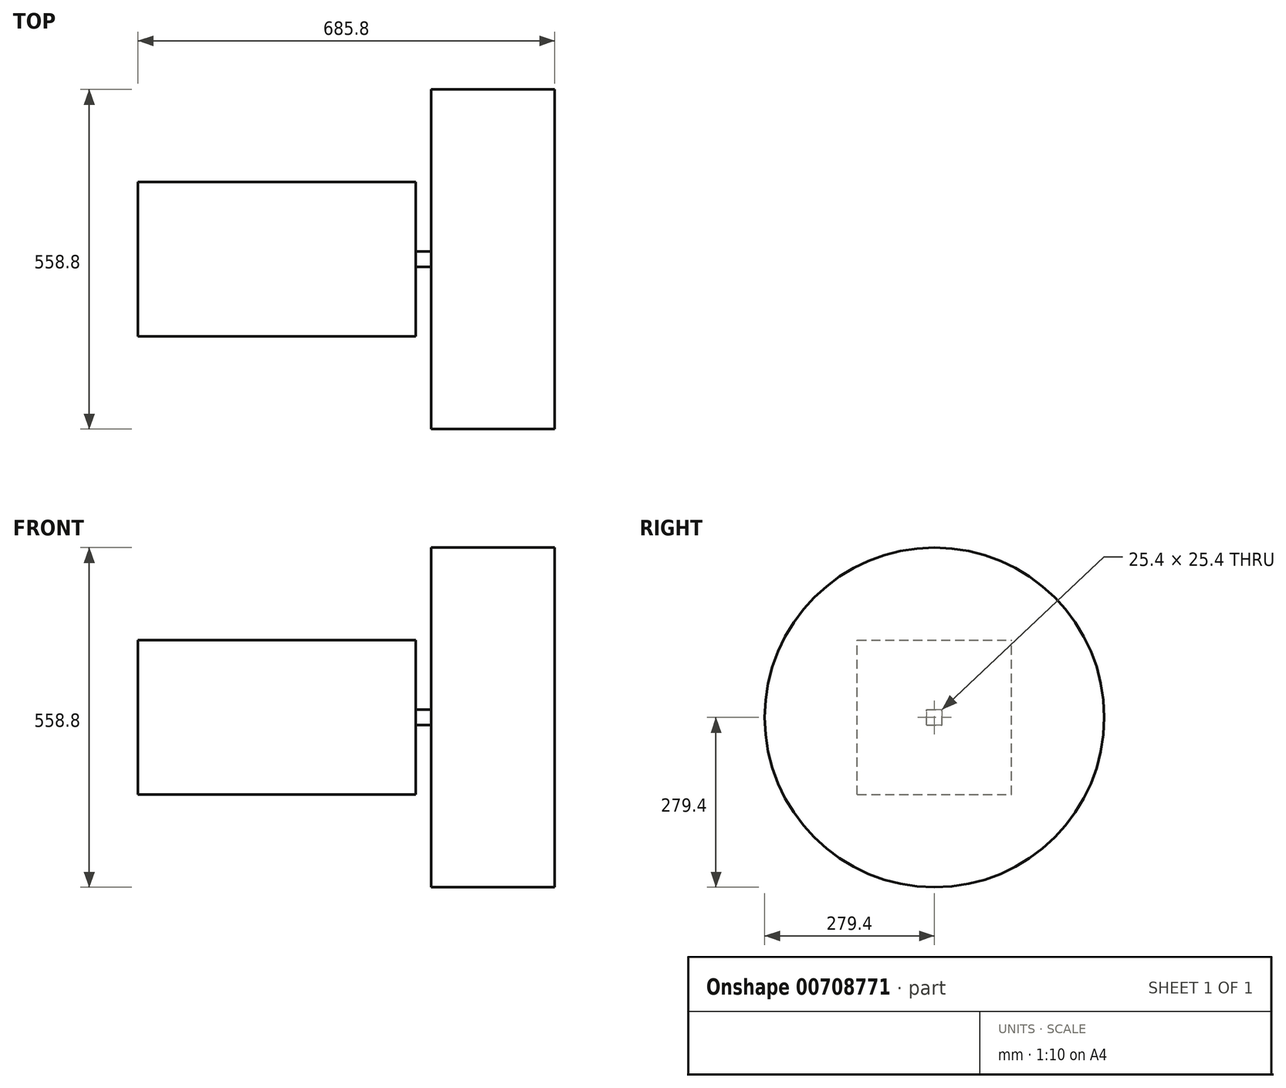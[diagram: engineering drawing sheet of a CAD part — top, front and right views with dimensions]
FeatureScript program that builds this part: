
annotation { "Feature Type Name" : "Feature", "Feature Type Description" : "" }
export const myFeature = defineFeature(function(context is Context, id is Id, definition is map)
    precondition{}
    {
        {
            var Q0;
            Q0=qCreatedBy(makeId("Front.planeOp"),FACE);
            var sketch = newSketch(context, id + "F0", { "sketchPlane" : qUnion([Q0])});
            skLineSegment(sketch, "E0.bottom", {"start": v(0, 0) * mm, "end": v(457.2, 0) * mm});
            skLineSegment(sketch, "E0.top", {"start": v(0, 254) * mm, "end": v(457.2, 254) * mm});
            skLineSegment(sketch, "E0.left", {"start": v(0, 0) * mm, "end": v(0, 254) * mm});
            skLineSegment(sketch, "E0.right", {"start": v(457.2, 0) * mm, "end": v(457.2, 254) * mm});
            skSolve(sketch);
        }
        {
            var Q0;
            Q0=makeQuery(id+"F0.imprint","IMPRINT",FACE,{"disambiguationData":[TD([[makeQuery(id+"F0.imprint","IMPRINT",EDGE,{"derivedFrom":sQuery(id+"F0.wireOp",EDGE,"E0.bottom")}),1.0]])]});
            extrude(context, id + "F1", {"entities" : qUnion([Q0]), "depth" : 254 * mm, "offsetDistance" : 25.4 * mm});
        }
        {
            var Q0;
            Q0=makeQuery(id+"F1.opExtrude","SWEPT_FACE",FACE,{"disambiguationData":[OSD([sQuery(id+"F0.wireOp",EDGE,"E0.right")])]});
            var sketch = newSketch(context, id + "F2", { "sketchPlane" : qUnion([Q0])});
            skLineSegment(sketch, "E1.bottom", {"start": v(-139.7, 114.3) * mm, "end": v(-114.3, 114.3) * mm});
            skLineSegment(sketch, "E1.top", {"start": v(-139.7, 139.7) * mm, "end": v(-114.3, 139.7) * mm});
            skLineSegment(sketch, "E1.left", {"start": v(-139.7, 114.3) * mm, "end": v(-139.7, 139.7) * mm});
            skLineSegment(sketch, "E1.right", {"start": v(-114.3, 114.3) * mm, "end": v(-114.3, 139.7) * mm});
            skSolve(sketch);
        }
        {
            var Q0;
            Q0 = qSketchRegion(id + "F2", true);
            extrude(context, id + "F3", {"entities" : qUnion([Q0]), "operationType" : NewBodyOperationType.ADD, "depth" : 25.4 * mm, "offsetDistance" : 25.4 * mm});
        }
        {
            var Q0;
            Q0=makeQuery(id+"F3.opExtrude","CAP_FACE",FACE,{"disambiguationData":[OSD([sQuery(id+"F2.wireOp",EDGE,"E1.bottom"),sQuery(id+"F2.wireOp",EDGE,"E1.top"),sQuery(id+"F2.wireOp",EDGE,"E1.left"),sQuery(id+"F2.wireOp",EDGE,"E1.right")])],"isStart":false});
            var sketch = newSketch(context, id + "F4", { "sketchPlane" : qUnion([Q0])});
            skPoint(sketch, "E2", {"position": v(-127, 127) * mm});
            skPoint(sketch, "E2.positionSnap0", {"position": v(-139.7, 127) * mm});
            skPoint(sketch, "E2.positionSnap1", {"position": v(-127, 139.7) * mm});
            skCircle(sketch, "E3", {"center": v(-127, 127) * mm, "radius": 279.4 * mm});
            skSolve(sketch);
        }
        {
            var Q0;
            Q0 = qSketchRegion(id + "F4", true);
            extrude(context, id + "F5", {"entities" : qUnion([Q0]), "operationType" : NewBodyOperationType.ADD, "depth" : 203.2 * mm, "offsetDistance" : 25.4 * mm});
        }
    });
